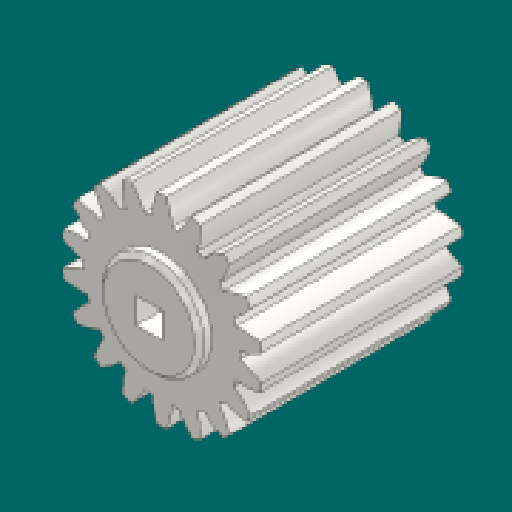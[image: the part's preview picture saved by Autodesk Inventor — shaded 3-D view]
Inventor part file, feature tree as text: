
AUTODESK INVENTOR PART (.ipt)
format: ipt  version: 2023.1 (Build 271208000, 208)  size: 297,472 bytes
history: native  units: mm (DEFAULTED — no unit token found)
features: sketch x5, extrude x4, plane x3, other x3, chamfer x2, projected_geometry x1
ambient origin geometry x8: Origin, YZ Plane, XZ Plane, XY Plane, X Axis, Y Axis, Z Axis, Center Point
bodies: Solid1 (feature_tree)
feature tree (18):
  extrude  "Extrusion1"  Depth=25.4mm TaperAngle=0.0deg
  plane  "Work Plane1"
  plane  "Work Plane2"
  plane  "Work Plane3"
  other  "Spur Gear"
  extrude  "Extrusion2"  Depth=76.2mm TaperAngle=0.0deg
  extrude  "Extrusion3"  TaperAngle=0.0deg  [1 undecoded]
  chamfer  "Chamfer1"  Distance=22.86mm
  extrude  "Extrusion4"  Depth=22.86mm TaperAngle=0.0deg
  chamfer  "Chamfer2"  Distance=3.302mm
  sketch  "Sketch1"  dims[d0=25.400062mm d1=25.4mm d2=0.0mm]
  sketch  "Sketch2"  dims[d3=22.86mm d4=76.2mm d5=0.0mm]
  other  "Srf1"
  sketch  "Sketch3"  dims[d6=0.0mm d7=1.745329mm d9=0.0mm d14=0.0mm d15=22.86mm]
  sketch  "Sketch4"  dims[d16=0.0mm d17=0.0mm d18=0.0mm d19=22.86mm]
  projected_geometry  "Projected Loop1"
  sketch  "Sketch5"  dims[d20=3.302mm d21=3.302mm d22=0.0mm d23=0.0mm d24=12.7mm d25=1.5875mm d26=0.0mm d27=0.6mm d28=3.175mm d29=45.0deg d30=6.604mm d31=6.604mm d32=23.8125mm d33=0.0mm d34=1.651mm d35=3.175mm d36=45.0deg]
  other  "Pitch Diameter"
note: 1 required parameter value undecoded (feature->parameter linkage not recoverable at this tier; creation-order binding heuristic only, values carry confidence <= 0.55)
